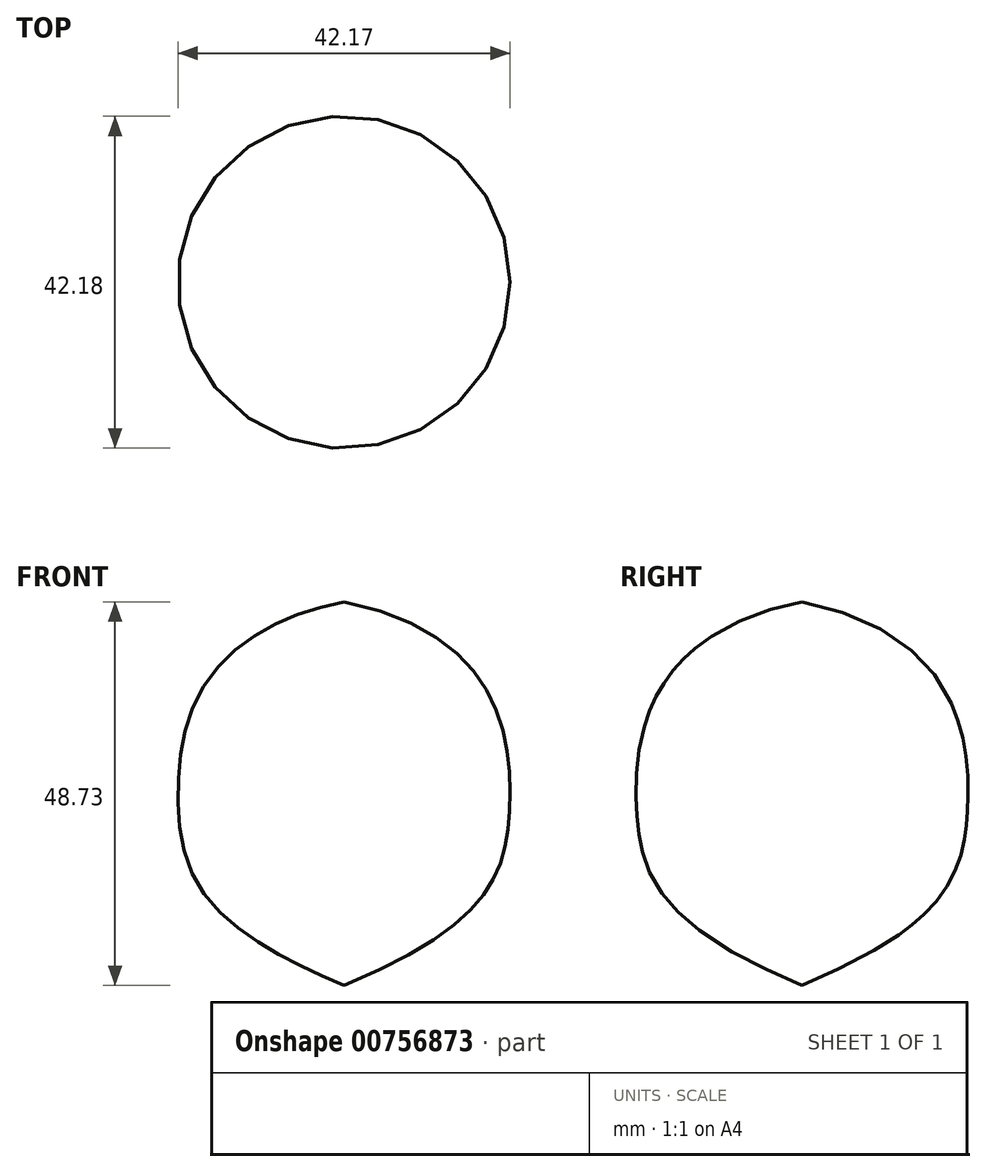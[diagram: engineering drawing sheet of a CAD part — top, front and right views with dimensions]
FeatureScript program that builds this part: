
annotation { "Feature Type Name" : "Feature", "Feature Type Description" : "" }
export const myFeature = defineFeature(function(context is Context, id is Id, definition is map)
    precondition{}
    {
        {
            var Q0;
            Q0=qCreatedBy(makeId("Front.planeOp"),FACE);
            var sketch = newSketch(context, id + "F0", { "sketchPlane" : qUnion([Q0])});
            skLineSegment(sketch, "E0", {"start": v(-41.66, 36.55) * mm, "end": v(-41.66, -12.18) * mm});
            skFitSpline(sketch, "E1", {"points": [v(-41.66, 36.55) * mm, v(-20.6, 10.68) * mm, v(-41.66, -12.18) * mm], "startDerivative": vector(113.5, -23.05) * mm, "endDerivative": vector(-110.23, -45.93) * mm});
            skSolve(sketch);
        }
        {
            var Q0;
            Q0=makeQuery(id+"F0.imprint","IMPRINT",FACE,{"disambiguationData":[TD([[makeQuery(id+"F0.imprint","IMPRINT",EDGE,{"derivedFrom":sQuery(id+"F0.wireOp",EDGE,"E0")}),1.0]])]});
            var Q1;
            Q1=sQuery(id+"F0.wireOp",EDGE,"E0");
            revolve(context, id + "F1", {"surfaceOperationType" : NewSurfaceOperationType.NEW, "entities" : qUnion([Q0]), "axis" : qUnion([Q1]), "revolveType" : RevolveType.FULL});
        }
    });
